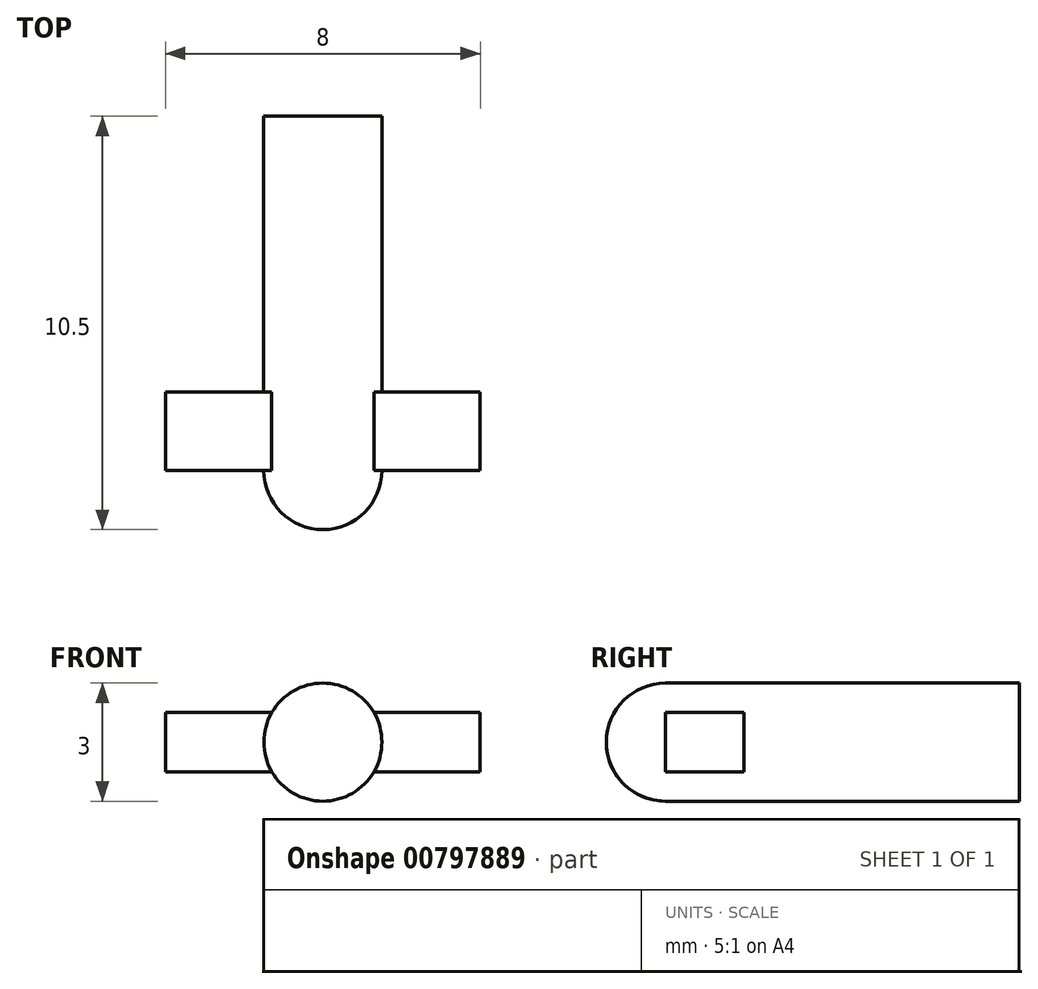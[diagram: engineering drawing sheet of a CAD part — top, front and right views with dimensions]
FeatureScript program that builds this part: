
annotation { "Feature Type Name" : "Feature", "Feature Type Description" : "" }
export const myFeature = defineFeature(function(context is Context, id is Id, definition is map)
    precondition{}
    {
        {
            var Q0;
            Q0=qCreatedBy(makeId("Front.planeOp"),FACE);
            var sketch = newSketch(context, id + "F0", { "sketchPlane" : qUnion([Q0])});
            skCircle(sketch, "E0", {"center": v(0, 0) * mm, "radius": 1.5 * mm});
            skSolve(sketch);
        }
        {
            var Q0;
            Q0 = qSketchRegion(id + "F0", true);
            extrude(context, id + "F1", {"entities" : qUnion([Q0]), "depth" : 7 * mm, "offsetDistance" : 25 * mm});
        }
        {
            var Q0;
            Q0=makeQuery(id+"F1.opExtrude","CAP_FACE",FACE,{"disambiguationData":[OSD([sQuery(id+"F0.wireOp",EDGE,"E0")])],"isStart":false});
            var sketch = newSketch(context, id + "F2", { "sketchPlane" : qUnion([Q0])});
            skCircle(sketch, "E1", {"center": v(0, 0) * mm, "radius": 1.5 * mm});
            skLineSegment(sketch, "E2.bottom", {"start": v(4, 0.75) * mm, "end": v(-4, 0.75) * mm});
            skLineSegment(sketch, "E2.top", {"start": v(4, -0.75) * mm, "end": v(-4, -0.75) * mm});
            skLineSegment(sketch, "E2.left", {"start": v(4, 0.75) * mm, "end": v(4, -0.75) * mm});
            skLineSegment(sketch, "E2.right", {"start": v(-4, 0.75) * mm, "end": v(-4, -0.75) * mm});
            skSolve(sketch);
        }
        {
            var Q0;
            Q0 = qSketchRegion(id + "F2", true);
            extrude(context, id + "F3", {"entities" : qUnion([Q0]), "operationType" : NewBodyOperationType.ADD, "depth" : 2 * mm, "offsetDistance" : 25 * mm});
        }
        {
            var Q0;
            Q0=makeQuery(id+"F3.opExtrude","CAP_FACE",FACE,{"disambiguationData":[OSD([sQuery(id+"F2.wireOp",EDGE,"E1"),sQuery(id+"F2.wireOp",EDGE,"E2.bottom"),sQuery(id+"F2.wireOp",EDGE,"E2.top"),sQuery(id+"F2.wireOp",EDGE,"E2.left"),sQuery(id+"F2.wireOp",EDGE,"E2.right")])],"isStart":false});
            var sketch = newSketch(context, id + "F4", { "sketchPlane" : qUnion([Q0])});
            skCircle(sketch, "E3", {"center": v(0, 0) * mm, "radius": 1.5 * mm});
            skSolve(sketch);
        }
        {
            var Q0;
            Q0 = qSketchRegion(id + "F4", true);
            extrude(context, id + "F5", {"entities" : qUnion([Q0]), "operationType" : NewBodyOperationType.ADD, "depth" : 1.5 * mm, "offsetDistance" : 25 * mm});
        }
        {
            var Q0;
            Q0=makeQuery(id+"F5.opExtrude","CAP_EDGE",EDGE,{"disambiguationData":[OSD([sQuery(id+"F4.wireOp",EDGE,"E3")])],"isStart":false});
            fillet(context, id + "F6", {"entities" : qUnion([Q0]), "radius" : 1.5 * mm, "tangentPropagation" : true, "allowEdgeOverflow" : false});
        }
    });
